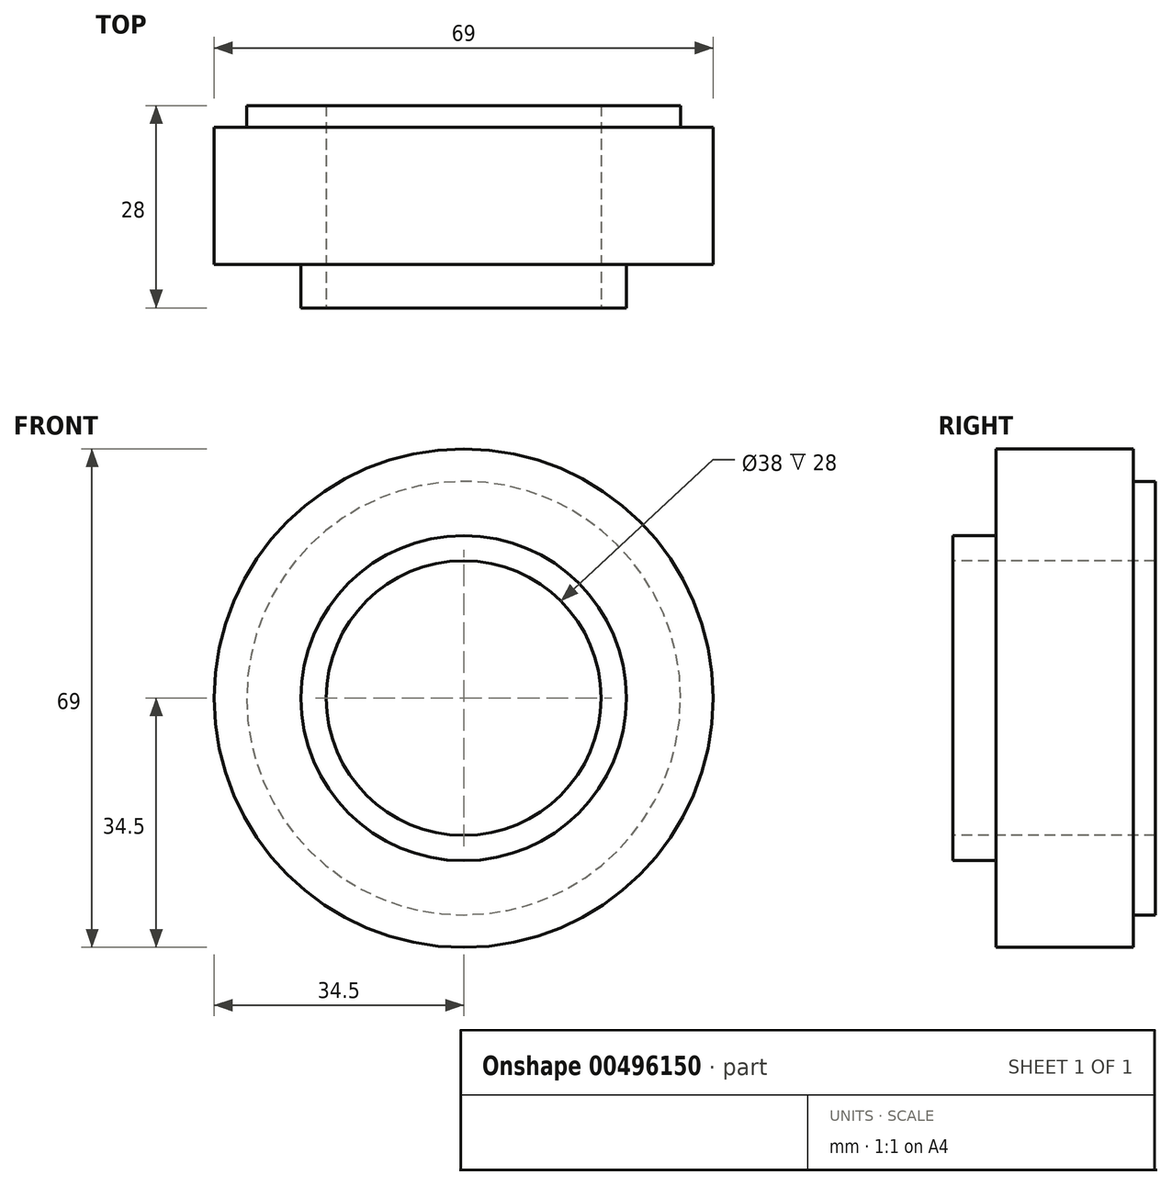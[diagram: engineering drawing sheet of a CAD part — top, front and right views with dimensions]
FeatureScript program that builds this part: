
annotation { "Feature Type Name" : "Feature", "Feature Type Description" : "" }
export const myFeature = defineFeature(function(context is Context, id is Id, definition is map)
    precondition{}
    {
        {
            var Q0;
            Q0=qCreatedBy(makeId("Front.planeOp"),FACE);
            var sketch = newSketch(context, id + "F0", { "sketchPlane" : qUnion([Q0])});
            skCircle(sketch, "E0", {"center": v(0, 0) * mm, "radius": 34.5 * mm});
            skSolve(sketch);
        }
        {
            var Q0;
            Q0 = qSketchRegion(id + "F0", true);
            extrude(context, id + "F1", {"entities" : qUnion([Q0]), "oppositeDirection" : true, "depth" : 19 * mm});
        }
        {
            var Q0;
            Q0=makeQuery(id+"F1.opExtrude","CAP_FACE",FACE,{"disambiguationData":[OSD([sQuery(id+"F0.wireOp",EDGE,"E0")])],"isStart":true});
            var sketch = newSketch(context, id + "F2", { "sketchPlane" : qUnion([Q0])});
            skCircle(sketch, "E1", {"center": v(0, 0) * mm, "radius": 22.5 * mm});
            skSolve(sketch);
        }
        {
            var Q0;
            Q0 = qSketchRegion(id + "F2", true);
            extrude(context, id + "F3", {"entities" : qUnion([Q0]), "operationType" : NewBodyOperationType.ADD, "depth" : 6 * mm});
        }
        {
            var Q0;
            Q0=makeQuery(id+"F1.opExtrude","CAP_FACE",FACE,{"disambiguationData":[OSD([sQuery(id+"F0.wireOp",EDGE,"E0")])],"isStart":false});
            var sketch = newSketch(context, id + "F4", { "sketchPlane" : qUnion([Q0])});
            skCircle(sketch, "E2", {"center": v(0, 0) * mm, "radius": 30 * mm});
            skSolve(sketch);
        }
        {
            var Q0;
            Q0 = qSketchRegion(id + "F4", true);
            extrude(context, id + "F5", {"entities" : qUnion([Q0]), "operationType" : NewBodyOperationType.ADD, "depth" : 3 * mm});
        }
        {
            var Q0;
            Q0=makeQuery(id+"F3.opExtrude","CAP_FACE",FACE,{"disambiguationData":[OSD([sQuery(id+"F2.wireOp",EDGE,"E1")])],"isStart":false});
            var sketch = newSketch(context, id + "F6", { "sketchPlane" : qUnion([Q0])});
            skCircle(sketch, "E3", {"center": v(0, 0) * mm, "radius": 19 * mm});
            skSolve(sketch);
        }
        {
            var Q0;
            Q0 = qSketchRegion(id + "F6", true);
            extrude(context, id + "F7", {"entities" : qUnion([Q0]), "operationType" : NewBodyOperationType.REMOVE, "oppositeDirection" : true, "depth" : 28 * mm});
        }
    });
